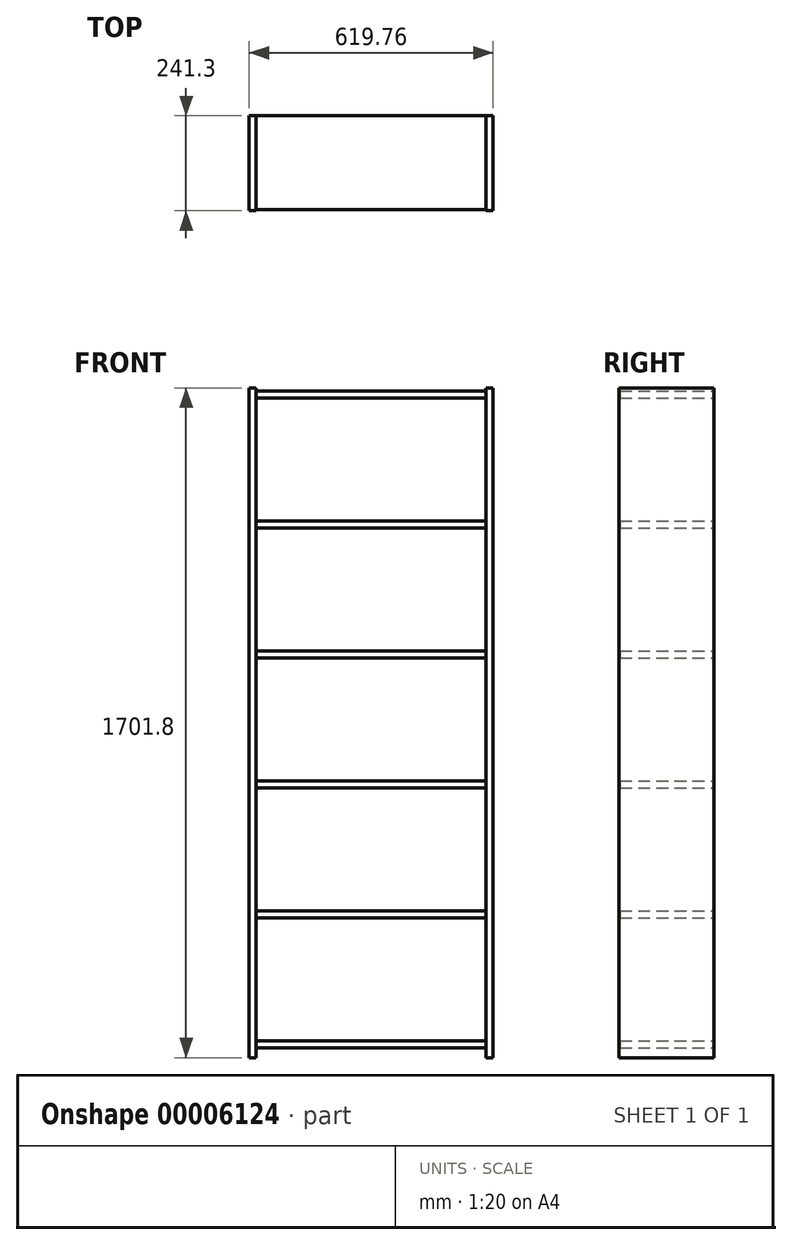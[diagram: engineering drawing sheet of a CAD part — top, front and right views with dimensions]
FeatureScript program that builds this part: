
annotation { "Feature Type Name" : "Feature", "Feature Type Description" : "" }
export const myFeature = defineFeature(function(context is Context, id is Id, definition is map)
    precondition{}
    {
        {
            var Q0;
            Q0=qCreatedBy(makeId("Front.planeOp"),FACE);
            var sketch = newSketch(context, id + "F0", { "sketchPlane" : qUnion([Q0])});
            skLineSegment(sketch, "E0.bottom", {"start": v(-41.31, 1650.2) * mm, "end": v(-23.53, 1650.2) * mm});
            skLineSegment(sketch, "E0.top", {"start": v(-41.31, -51.6) * mm, "end": v(-23.53, -51.6) * mm});
            skLineSegment(sketch, "E0.left", {"start": v(-41.31, 1650.2) * mm, "end": v(-41.31, -51.6) * mm});
            skLineSegment(sketch, "E0.right", {"start": v(-23.53, 1650.2) * mm, "end": v(-23.53, -51.6) * mm});
            skLineSegment(sketch, "E1.bottom", {"start": v(-23.53, -26.2) * mm, "end": v(560.67, -26.2) * mm});
            skLineSegment(sketch, "E1.top", {"start": v(-23.53, -8.42) * mm, "end": v(560.67, -8.42) * mm});
            skLineSegment(sketch, "E1.left", {"start": v(-23.53, -26.2) * mm, "end": v(-23.53, -8.42) * mm});
            skLineSegment(sketch, "E1.right", {"start": v(560.67, -26.2) * mm, "end": v(560.67, -8.42) * mm});
            skLineSegment(sketch, "E2", {"start": v(268.57, -8.42) * mm, "end": v(268.57, 1645.27) * mm, "construction": true});
            skLineSegment(sketch, "E3.1.MirrorCS", {"start": v(560.67, 1650.2) * mm, "end": v(560.67, -51.6) * mm});
            skLineSegment(sketch, "E3.2.MirrorCS", {"start": v(578.45, 1650.2) * mm, "end": v(560.67, 1650.2) * mm});
            skLineSegment(sketch, "E3.3.MirrorCS", {"start": v(578.45, -51.6) * mm, "end": v(560.67, -51.6) * mm});
            skLineSegment(sketch, "E3.4.MirrorCS", {"start": v(578.45, 1650.2) * mm, "end": v(578.45, -51.6) * mm});
            skLineSegment(sketch, "E4.0.1.0", {"start": v(560.67, 304) * mm, "end": v(560.67, 321.78) * mm});
            skLineSegment(sketch, "E4.0.1.1", {"start": v(-23.53, 304) * mm, "end": v(560.67, 304) * mm});
            skLineSegment(sketch, "E4.0.1.2", {"start": v(-23.53, 304) * mm, "end": v(-23.53, 321.78) * mm});
            skLineSegment(sketch, "E4.0.1.3", {"start": v(-23.53, 321.78) * mm, "end": v(560.67, 321.78) * mm});
            skLineSegment(sketch, "E4.0.1.4", {"start": v(560.67, 304) * mm, "end": v(560.67, 321.78) * mm});
            skLineSegment(sketch, "E4.0.2.0", {"start": v(560.67, 634.2) * mm, "end": v(560.67, 651.98) * mm});
            skLineSegment(sketch, "E4.0.2.1", {"start": v(-23.53, 634.2) * mm, "end": v(560.67, 634.2) * mm});
            skLineSegment(sketch, "E4.0.2.2", {"start": v(-23.53, 634.2) * mm, "end": v(-23.53, 651.98) * mm});
            skLineSegment(sketch, "E4.0.2.3", {"start": v(-23.53, 651.98) * mm, "end": v(560.67, 651.98) * mm});
            skLineSegment(sketch, "E4.0.2.4", {"start": v(560.67, 634.2) * mm, "end": v(560.67, 651.98) * mm});
            skLineSegment(sketch, "E4.0.3.0", {"start": v(560.67, 964.4) * mm, "end": v(560.67, 982.18) * mm});
            skLineSegment(sketch, "E4.0.3.1", {"start": v(-23.53, 964.4) * mm, "end": v(560.67, 964.4) * mm});
            skLineSegment(sketch, "E4.0.3.2", {"start": v(-23.53, 964.4) * mm, "end": v(-23.53, 982.18) * mm});
            skLineSegment(sketch, "E4.0.3.3", {"start": v(-23.53, 982.18) * mm, "end": v(560.67, 982.18) * mm});
            skLineSegment(sketch, "E4.0.3.4", {"start": v(560.67, 964.4) * mm, "end": v(560.67, 982.18) * mm});
            skLineSegment(sketch, "E4.0.4.0", {"start": v(560.67, 1294.6) * mm, "end": v(560.67, 1312.38) * mm});
            skLineSegment(sketch, "E4.0.4.1", {"start": v(-23.53, 1294.6) * mm, "end": v(560.67, 1294.6) * mm});
            skLineSegment(sketch, "E4.0.4.2", {"start": v(-23.53, 1294.6) * mm, "end": v(-23.53, 1312.38) * mm});
            skLineSegment(sketch, "E4.0.4.3", {"start": v(-23.53, 1312.38) * mm, "end": v(560.67, 1312.38) * mm});
            skLineSegment(sketch, "E4.0.4.4", {"start": v(560.67, 1294.6) * mm, "end": v(560.67, 1312.38) * mm});
            skLineSegment(sketch, "E4.0.5.0", {"start": v(560.67, 1624.8) * mm, "end": v(560.67, 1642.58) * mm});
            skLineSegment(sketch, "E4.0.5.1", {"start": v(-23.53, 1624.8) * mm, "end": v(560.67, 1624.8) * mm});
            skLineSegment(sketch, "E4.0.5.2", {"start": v(-23.53, 1624.8) * mm, "end": v(-23.53, 1642.58) * mm});
            skLineSegment(sketch, "E4.0.5.3", {"start": v(-23.53, 1642.58) * mm, "end": v(560.67, 1642.58) * mm});
            skLineSegment(sketch, "E4.0.5.4", {"start": v(560.67, 1624.8) * mm, "end": v(560.67, 1642.58) * mm});
            skLineSegment(sketch, "E4.direction1", {"start": v(560.67, -26.2) * mm, "end": v(586.07, -26.2) * mm, "construction": true});
            skLineSegment(sketch, "E4.direction2", {"start": v(560.67, -26.2) * mm, "end": v(560.67, 304) * mm, "construction": true});
            skSolve(sketch);
        }
        {
            var Q0;
            {var subQ8=sQuery(id+"F0.wireOp",EDGE,"E0.bottom");Q0=makeQuery(id+"F0.imprint","IMPRINT",FACE,{"disambiguationData":[TD([[makeQuery(id+"F0.imprint","IMPRINT",EDGE,{"derivedFrom":subQ8}),-1.0]])]});}
            var Q1;
            {var subQ9=sQuery(id+"F0.wireOp",EDGE,"E3.2.MirrorCS");Q1=makeQuery(id+"F0.imprint","IMPRINT",FACE,{"disambiguationData":[TD([[makeQuery(id+"F0.imprint","IMPRINT",EDGE,{"derivedFrom":subQ9}),1.0]])]});}
            var Q2;
            Q2=sQuery(id+"F0.wireOp",EDGE,"E4.0.5.2");
            var Q3;
            Q3=sQuery(id+"F0.wireOp",EDGE,"E0.left");
            var Q4;
            Q4=sQuery(id+"F0.wireOp",EDGE,"E0.top");
            var Q5;
            Q5=sQuery(id+"F0.wireOp",EDGE,"E0.right");
            var Q6;
            Q6=sQuery(id+"F0.wireOp",EDGE,"E4.0.1.2");
            var Q7;
            Q7=sQuery(id+"F0.wireOp",EDGE,"E4.0.3.2");
            var Q8;
            Q8=sQuery(id+"F0.wireOp",EDGE,"E4.0.2.2");
            var Q9;
            Q9=sQuery(id+"F0.wireOp",EDGE,"E4.0.4.2");
            var Q10;
            Q10=sQuery(id+"F0.wireOp",EDGE,"E0.bottom");
            var Q11;
            Q11=sQuery(id+"F0.wireOp",EDGE,"E1.left");
            var Q12;
            Q12=sQuery(id+"F0.wireOp",EDGE,"E1.right");
            var Q13;
            Q13=sQuery(id+"F0.wireOp",EDGE,"E3.1.MirrorCS");
            var Q14;
            Q14=sQuery(id+"F0.wireOp",EDGE,"E3.4.MirrorCS");
            var Q15;
            Q15=sQuery(id+"F0.wireOp",EDGE,"E1.right");
            var Q16;
            Q16=sQuery(id+"F0.wireOp",EDGE,"E3.2.MirrorCS");
            var Q17;
            Q17=sQuery(id+"F0.wireOp",EDGE,"E4.direction2");
            var Q18;
            Q18=sQuery(id+"F0.wireOp",EDGE,"E4.0.2.4");
            var Q19;
            Q19=sQuery(id+"F0.wireOp",EDGE,"E4.0.4.0");
            var Q20;
            Q20=sQuery(id+"F0.wireOp",EDGE,"E4.0.5.4");
            var Q21;
            Q21=sQuery(id+"F0.wireOp",EDGE,"E3.3.MirrorCS");
            var Q22;
            Q22=sQuery(id+"F0.wireOp",EDGE,"E4.0.3.0");
            var Q23;
            Q23=sQuery(id+"F0.wireOp",EDGE,"E4.0.1.0");
            var Q24;
            Q24=sQuery(id+"F0.wireOp",EDGE,"E4.0.2.0");
            var Q25;
            Q25=sQuery(id+"F0.wireOp",EDGE,"E4.0.4.4");
            var Q26;
            Q26=sQuery(id+"F0.wireOp",EDGE,"E4.0.5.0");
            var Q27;
            Q27=sQuery(id+"F0.wireOp",EDGE,"E4.0.1.4");
            var Q28;
            Q28=sQuery(id+"F0.wireOp",EDGE,"E4.0.3.4");
            var Q29;
            Q29=sQuery(id+"F0.wireOp",EDGE,"E4.direction1");
            extrude(context, id + "F1", {"entities" : qUnion([Q0, Q1]), "surfaceEntities" : qUnion([Q2, Q3, Q4, Q5, Q6, Q7, Q8, Q9, Q10, Q11, Q12, Q13, Q14, Q15, Q16, Q17, Q18, Q19, Q20, Q21, Q22, Q23, Q24, Q25, Q26, Q27, Q28, Q29]), "depth" : 241.3 * mm});
        }
        {
            var Q0;
            {var subQ2=sQuery(id+"F0.wireOp",EDGE,"E1.bottom");Q0=makeQuery(id+"F0.imprint","IMPRINT",FACE,{"disambiguationData":[TD([[makeQuery(id+"F0.imprint","IMPRINT",EDGE,{"derivedFrom":subQ2}),1.0]])]});}
            var Q1;
            Q1=makeQuery(id+"F0.imprint","IMPRINT",FACE,{"disambiguationData":[TD([[makeQuery(id+"F0.imprint","IMPRINT",EDGE,{"derivedFrom":sQuery(id+"F0.wireOp",EDGE,"E4.0.1.1")}),1.0]])]});
            var Q2;
            Q2=makeQuery(id+"F0.imprint","IMPRINT",FACE,{"disambiguationData":[TD([[makeQuery(id+"F0.imprint","IMPRINT",EDGE,{"derivedFrom":sQuery(id+"F0.wireOp",EDGE,"E4.0.2.1")}),1.0]])]});
            var Q3;
            Q3=makeQuery(id+"F0.imprint","IMPRINT",FACE,{"disambiguationData":[TD([[makeQuery(id+"F0.imprint","IMPRINT",EDGE,{"derivedFrom":sQuery(id+"F0.wireOp",EDGE,"E4.0.3.1")}),1.0]])]});
            var Q4;
            Q4=makeQuery(id+"F0.imprint","IMPRINT",FACE,{"disambiguationData":[TD([[makeQuery(id+"F0.imprint","IMPRINT",EDGE,{"derivedFrom":sQuery(id+"F0.wireOp",EDGE,"E4.0.4.1")}),1.0]])]});
            var Q5;
            Q5=makeQuery(id+"F0.imprint","IMPRINT",FACE,{"disambiguationData":[TD([[makeQuery(id+"F0.imprint","IMPRINT",EDGE,{"derivedFrom":sQuery(id+"F0.wireOp",EDGE,"E4.0.5.1")}),1.0]])]});
            extrude(context, id + "F2", {"entities" : qUnion([Q0, Q1, Q2, Q3, Q4, Q5]), "operationType" : NewBodyOperationType.ADD, "depth" : 238.76 * mm});
        }
    });
